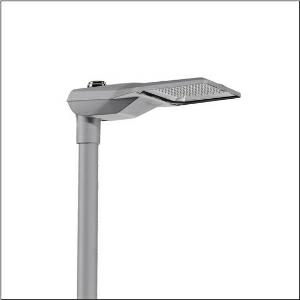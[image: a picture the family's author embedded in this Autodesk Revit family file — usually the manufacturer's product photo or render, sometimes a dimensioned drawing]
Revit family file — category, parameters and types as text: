
# Revit family: streetlight_sl_21_midi___st0_5a_5xe7b37n08lb_6898
name_source: partatom
category: Lighting Fixtures
units: mm (PartAtom-declared; Revit-internal decimal feet)

## family parameters
Cut with Voids When Loaded = No
Host = Face
Light Source = No
Part Type = Normal
Room Calculation Point = No
Round Connector Dimension = Use Diameter
Shared = No

## types (1)
- --- (1 x LED, 14340 lm, 98.3 W, 3000K)
    Apparent Load = 98 VA
    CIE Flux Codes = 41 75 97 100 100
    Color Rendering = 70
    Color Temperature = 3000K
    Default Elevation = 1800 mm
    Description = Streetlight SL 21 midi, mast luminaire, primary light control with lens, of PMMA, primary optical cover: cover, of toughened safety glass, transparent, light distribution: ST0.5a, light emission: direct distribution, primary light characteristic: asymmetric, installation type: side-entry, LED, 3G 2.5mm², High Power LED, rated luminous flux: 14.340lm, luminous efficacy: 146lm/W, light colour: 730, colour temperature: 3000K, control gear: NEMA (7pin), control: overheat protection, pre-setting: linear dimming characteristic, constant luminous flux control, time-dependent luminous flux control, flexible luminous flux parameterisation, mains connection: 220..240V, AC, 50/60Hz, connection cable pre-assembled, cable length: 10,5m, wiring characteristics: H05VV-F, start of lifetime: 98W, end of service life: 101W, reduction: 45W, luminaire housing, of diecast aluminium (EN AC-44300), powder-coated, SITECO metallic grey (DB 702S), corrosivity category C5 high according to DIN EN ISO 12944, multi-level sealing system, sealing non-destructively replaceable, inclination adjustable: 0°, 5°, 10°, 15°, length: 644mm, width: 335mm, height: 110mm, spigot size: 42mm (side-entry), mounting height: 4..8m, protection rating (complete): IP66, insulation class (complete): insulation class I (protective earthing), certification: CE, ENEC, ENEC+, VDE, impact resistance: IK10, permissible operating ambient temperature for outdoor applications: -40..+50°C, standard-compliant lighting for roads and squares, packaging unit: 1 piece

Light Distribution: ST0.5a
    Height = 111 mm
    Lamp = 1 x LED
    Lamp Light Flux = 14340 lm
    Lamp Power = 98.3 W
    Lamp count = 1
    Length = 644 mm
    Luminous efficacy = 146 lm/W
    Manufacturer = Siteco
    ModVariant = No
    Model = 5XE7B37N08LB
    Number of Poles = 1
    OnlyDefault = Yes
    Power Factor = 1
    Product Name = Streetlight SL 21 midi | ST0.5a
    Product group = mast luminaire | pylon top
    ProductGroupID = 6100
    Protection Class = Protection class I
    Protection Degree = IP 66
    RLX_Detail_Level = 1
    RLX_Emergency_Light_Flux = 0 lm
    RLX_Emergency_Type = 0
    RLX_Emergency_Type_DB = No
    RlxData = <blob elided: 37725 chars, md5=7b6f6da0>
    Socket = socket
    Standby Power = 0 W
    System Light Flux = 14340 lm
    System Power = 98 W
    Type Comments = factory setting: luminous flux: 100 % | dim-lin: 254 | 1020 mA
    Type Image = l_1294377.jpg
    URL = http://relux.com
    VarID = @adj_136873
    Voltage = 0 V
    Weight = 0.00 kg
    Width = 336 mm

## geometry (parser evidence)
native form markers: Blend x4, Sweep x9
no freeform markers — native parametric forms only
